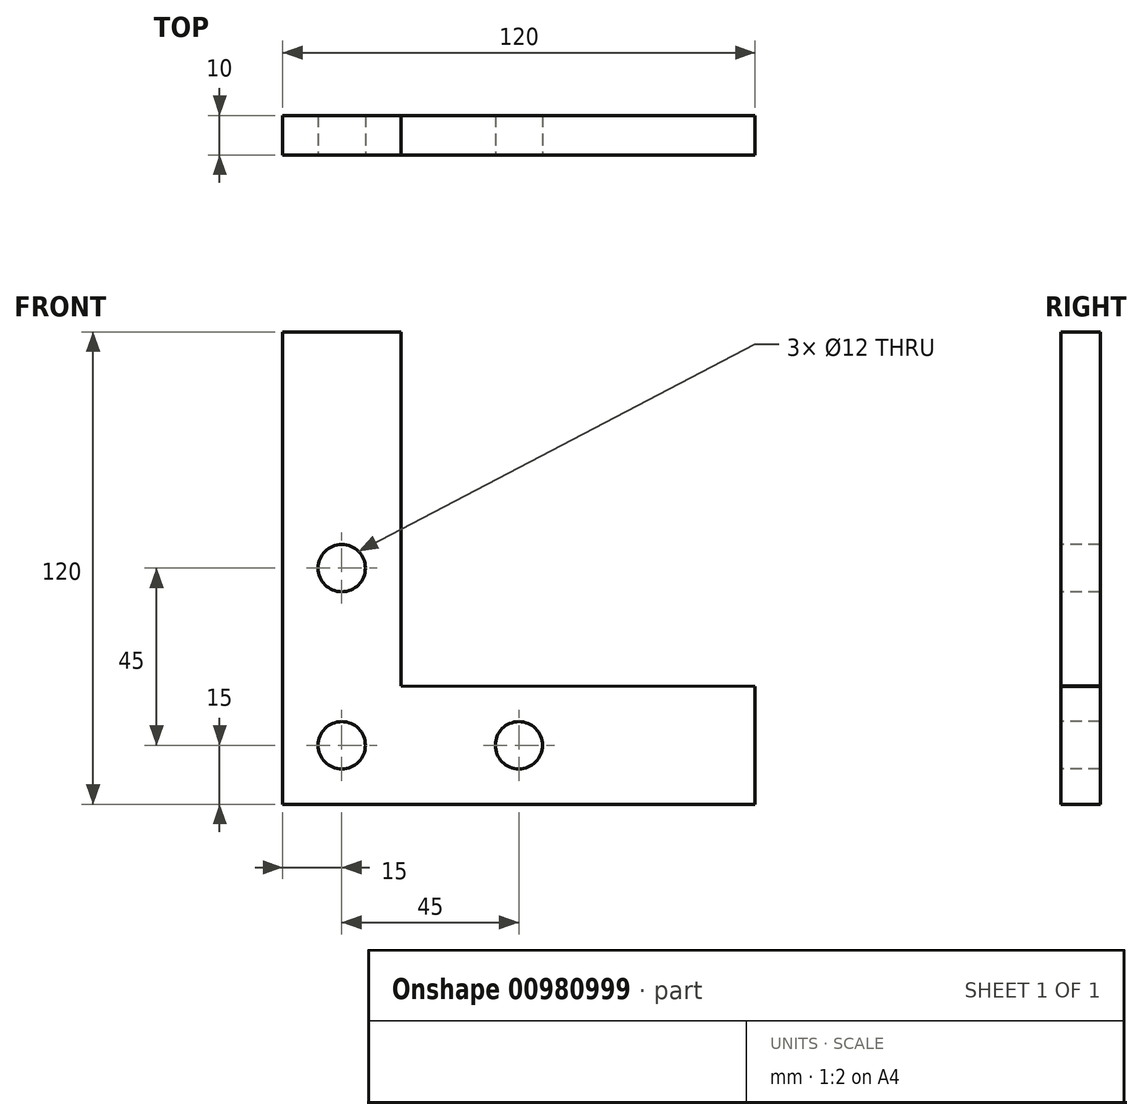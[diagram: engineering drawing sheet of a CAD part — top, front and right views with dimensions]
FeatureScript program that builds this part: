
annotation { "Feature Type Name" : "Feature", "Feature Type Description" : "" }
export const myFeature = defineFeature(function(context is Context, id is Id, definition is map)
    precondition{}
    {
        {
            var Q0;
            Q0=qCreatedBy(makeId("Front.planeOp"),FACE);
            var sketch = newSketch(context, id + "F0", { "sketchPlane" : qUnion([Q0])});
            skLineSegment(sketch, "E0.bottom", {"start": v(60, 60) * mm, "end": v(-60, 60) * mm});
            skLineSegment(sketch, "E0.top", {"start": v(60, -60) * mm, "end": v(-60, -60) * mm});
            skLineSegment(sketch, "E0.left", {"start": v(60, 60) * mm, "end": v(60, -60) * mm});
            skLineSegment(sketch, "E0.right", {"start": v(-60, 60) * mm, "end": v(-60, -60) * mm});
            skPoint(sketch, "E0.middle", {"position": v(0, 0) * mm});
            skLineSegment(sketch, "E1", {"start": v(-60, 60) * mm, "end": v(-30, 60) * mm});
            skLineSegment(sketch, "E2", {"start": v(-30, 60) * mm, "end": v(-30, -29.92) * mm});
            skLineSegment(sketch, "E3", {"start": v(60, -60) * mm, "end": v(60, -30) * mm});
            skLineSegment(sketch, "E4", {"start": v(60, -30) * mm, "end": v(-30, -29.92) * mm});
            skCircle(sketch, "E5", {"center": v(-45, -45) * mm, "radius": 6 * mm});
            skPoint(sketch, "E5.centerSnap0", {"position": v(60, -45) * mm});
            skPoint(sketch, "E5.centerSnap1", {"position": v(-45, 60) * mm});
            skCircle(sketch, "E6", {"center": v(0, -45) * mm, "radius": 6 * mm});
            skCircle(sketch, "E7", {"center": v(-45, 0) * mm, "radius": 6 * mm});
            skSolve(sketch);
        }
        {
            var Q0;
            Q0=makeQuery(id+"F0.imprint","IMPRINT",FACE,{"disambiguationData":[TD([[makeQuery(id+"F0.imprint","IMPRINT",EDGE,{"derivedFrom":sQuery(id+"F0.wireOp",EDGE,"E0.top")}),-1.0]])]});
            extrude(context, id + "F1", {"entities" : qUnion([Q0]), "oppositeDirection" : true, "depth" : 10 * mm, "offsetDistance" : 25 * mm});
        }
    });
